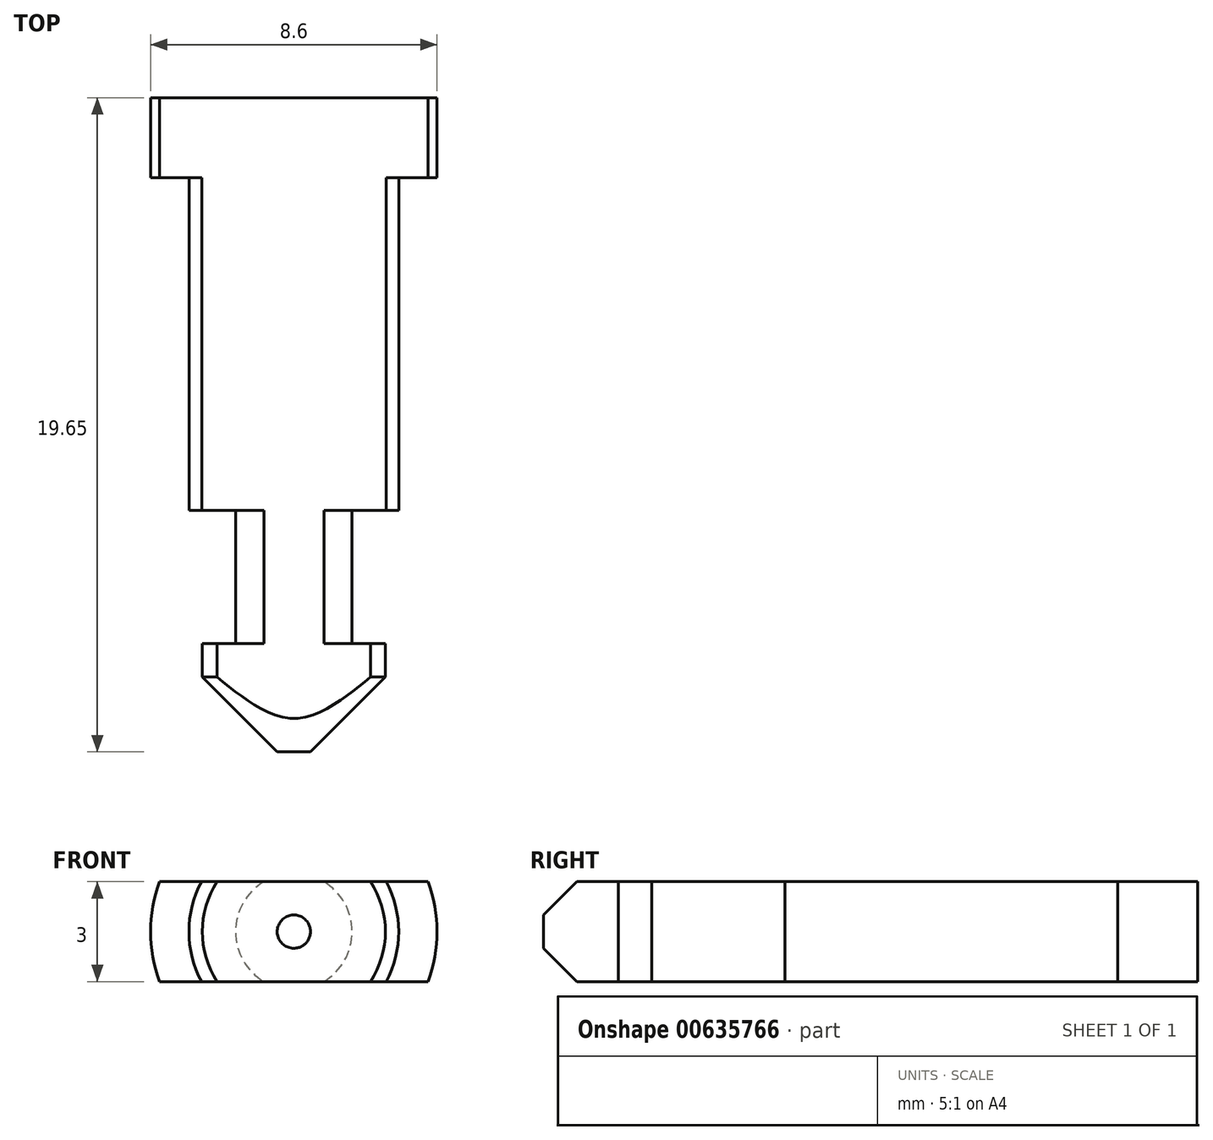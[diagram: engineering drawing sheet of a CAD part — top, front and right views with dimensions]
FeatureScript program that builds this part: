
annotation { "Feature Type Name" : "Feature", "Feature Type Description" : "" }
export const myFeature = defineFeature(function(context is Context, id is Id, definition is map)
    precondition{}
    {
        {
            var Q0;
            Q0=qCreatedBy(makeId("Top.planeOp"),FACE);
            var sketch = newSketch(context, id + "F0", { "sketchPlane" : qUnion([Q0])});
            skLineSegment(sketch, "E0", {"start": v(0, 0) * mm, "end": v(0, 19.65) * mm});
            skLineSegment(sketch, "E1", {"start": v(0, 0) * mm, "end": v(0.5, 0) * mm});
            skLineSegment(sketch, "E2", {"start": v(2.75, 3.25) * mm, "end": v(1.75, 3.25) * mm});
            skLineSegment(sketch, "E3", {"start": v(1.75, 3.25) * mm, "end": v(1.75, 7.25) * mm});
            skLineSegment(sketch, "E4", {"start": v(1.75, 7.25) * mm, "end": v(3.15, 7.25) * mm});
            skLineSegment(sketch, "E5", {"start": v(3.15, 7.25) * mm, "end": v(3.15, 17.25) * mm});
            skLineSegment(sketch, "E6", {"start": v(3.15, 17.25) * mm, "end": v(4.3, 17.25) * mm});
            skLineSegment(sketch, "E7", {"start": v(4.3, 17.25) * mm, "end": v(4.3, 19.65) * mm});
            skLineSegment(sketch, "E8", {"start": v(4.3, 19.65) * mm, "end": v(0, 19.65) * mm});
            skLineSegment(sketch, "E9", {"start": v(2.75, 3.25) * mm, "end": v(2.75, 2.25) * mm});
            skLineSegment(sketch, "E10", {"start": v(2.75, 2.25) * mm, "end": v(0.5, 0) * mm});
            skSolve(sketch);
        }
        {
            var Q0;
            Q0=makeQuery(id+"F0.imprint","IMPRINT",FACE,{"disambiguationData":[TD([[makeQuery(id+"F0.imprint","IMPRINT",EDGE,{"derivedFrom":sQuery(id+"F0.wireOp",EDGE,"E0")}),-1.0]])]});
            var Q1;
            Q1=sQuery(id+"F0.wireOp",EDGE,"E0");
            revolve(context, id + "F1", {"entities" : qUnion([Q0]), "axis" : qUnion([Q1]), "revolveType" : RevolveType.FULL});
        }
        {
            var Q0;
            Q0=makeQuery(id+"F1.opRevolve","SWEPT_FACE",FACE,{"disambiguationData":[OSD([sQuery(id+"F0.wireOp",EDGE,"E8")])]});
            var sketch = newSketch(context, id + "F2", { "sketchPlane" : qUnion([Q0])});
            skLineSegment(sketch, "E11.bottom", {"start": v(7.5, 1.5) * mm, "end": v(-7.5, 1.5) * mm});
            skLineSegment(sketch, "E11.top", {"start": v(7.5, -1.5) * mm, "end": v(-7.5, -1.5) * mm});
            skLineSegment(sketch, "E11.left", {"start": v(7.5, 1.5) * mm, "end": v(7.5, -1.5) * mm});
            skLineSegment(sketch, "E11.right", {"start": v(-7.5, 1.5) * mm, "end": v(-7.5, -1.5) * mm});
            skPoint(sketch, "E11.middle", {"position": v(0, 0) * mm});
            skSolve(sketch);
        }
        {
            var Q0;
            Q0 = qSketchRegion(id + "F2", true);
            extrude(context, id + "F3", {"entities" : qUnion([Q0]), "oppositeDirection" : true, "depth" : 25 * mm, "offsetDistance" : 25 * mm});
        }
        {
            var Q0;
            Q0=makeQuery(id+"F3.opExtrude","SWEPT_BODY",BODY,{"disambiguationData":[OSD([sQuery(id+"F2.wireOp",EDGE,"E11.bottom"),sQuery(id+"F2.wireOp",EDGE,"E11.top"),sQuery(id+"F2.wireOp",EDGE,"E11.left"),sQuery(id+"F2.wireOp",EDGE,"E11.right")])]});
            var Q1;
            Q1=makeQuery(id+"F1.opRevolve","SWEPT_BODY",BODY,{"disambiguationData":[OSD([sQuery(id+"F0.wireOp",EDGE,"E0"),sQuery(id+"F0.wireOp",EDGE,"E1"),sQuery(id+"F0.wireOp",EDGE,"E2"),sQuery(id+"F0.wireOp",EDGE,"E3"),sQuery(id+"F0.wireOp",EDGE,"E4"),sQuery(id+"F0.wireOp",EDGE,"E5"),sQuery(id+"F0.wireOp",EDGE,"E6"),sQuery(id+"F0.wireOp",EDGE,"E7"),sQuery(id+"F0.wireOp",EDGE,"E8"),sQuery(id+"F0.wireOp",EDGE,"E9"),sQuery(id+"F0.wireOp",EDGE,"E10")])]});
            booleanBodies(context, id + "F4", {"operationType" : BooleanOperationType.INTERSECTION, "tools" : qUnion([Q0, Q1])});
        }
    });
